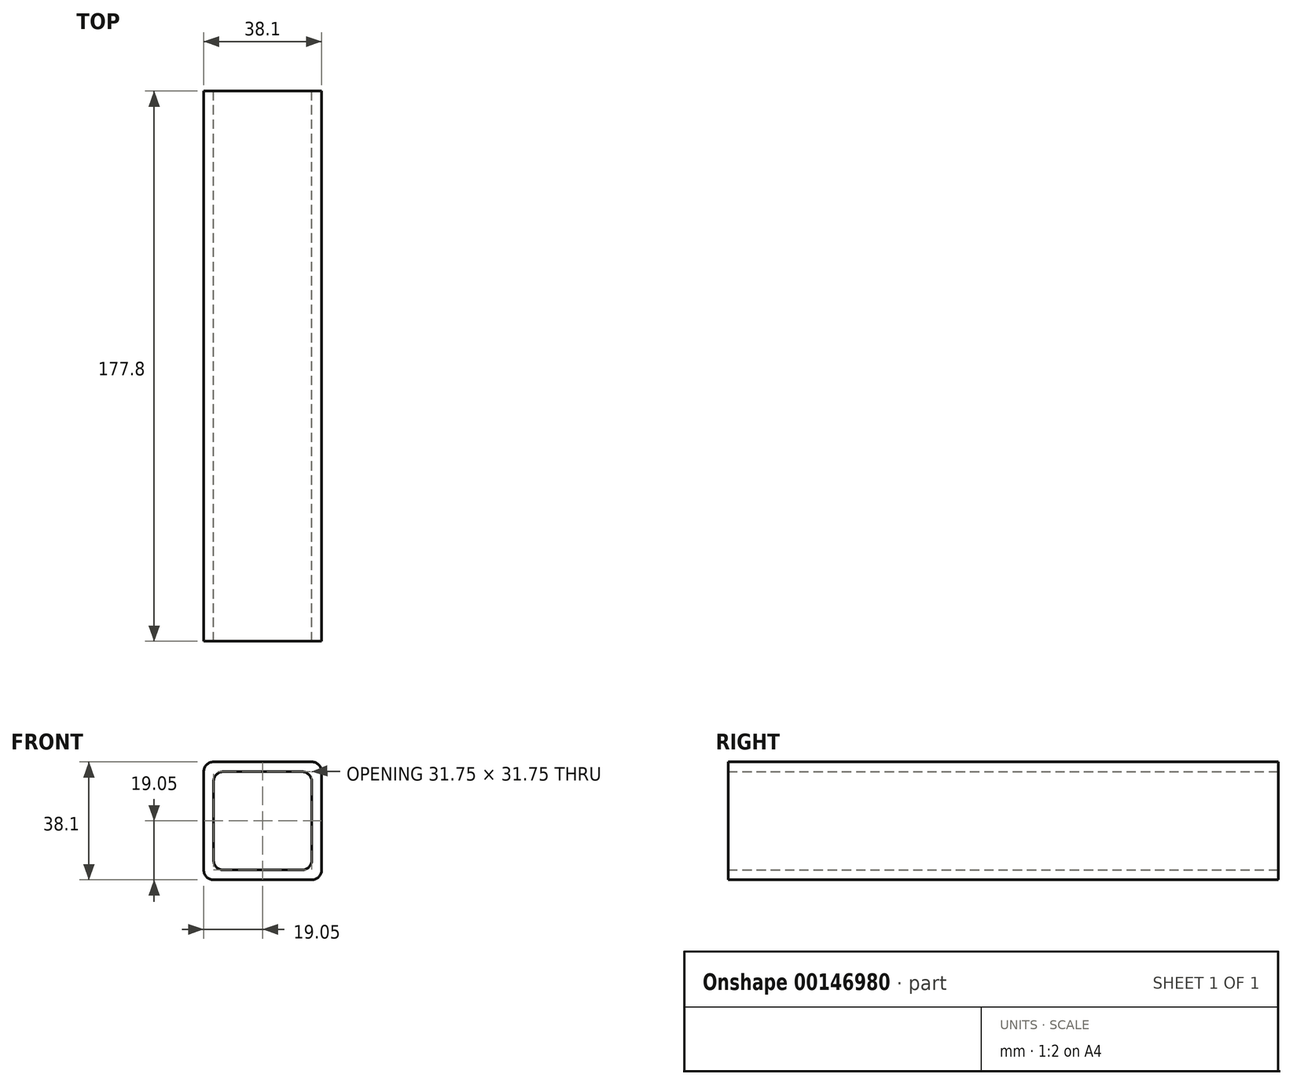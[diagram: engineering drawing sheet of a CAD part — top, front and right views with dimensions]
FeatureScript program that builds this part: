
annotation { "Feature Type Name" : "Feature", "Feature Type Description" : "" }
export const myFeature = defineFeature(function(context is Context, id is Id, definition is map)
    precondition{}
    {
        {
            var Q0;
            Q0=qCreatedBy(makeId("Front.planeOp"),FACE);
            var sketch = newSketch(context, id + "F0", { "sketchPlane" : qUnion([Q0])});
            skLineSegment(sketch, "E0.bottom", {"start": v(15.87, 19.05) * mm, "end": v(-15.87, 19.05) * mm});
            skLineSegment(sketch, "E0.top", {"start": v(15.87, -19.05) * mm, "end": v(-15.87, -19.05) * mm});
            skLineSegment(sketch, "E0.left", {"start": v(19.05, 15.87) * mm, "end": v(19.05, -15.87) * mm});
            skLineSegment(sketch, "E0.right", {"start": v(-19.05, 15.87) * mm, "end": v(-19.05, -15.87) * mm});
            skPoint(sketch, "E0.middle", {"position": v(0, 0) * mm});
            skPoint(sketch, "E1.visualSharp", {"position": v(-19.05, 19.05) * mm});
            skArc(sketch, "E1.filletArc", {"start": v(-15.87, 19.05) * mm, "mid": v(-18.12, 18.12) * mm, "end": v(-19.05, 15.87) * mm});
            skPoint(sketch, "E2.visualSharp", {"position": v(19.05, 19.05) * mm});
            skArc(sketch, "E2.filletArc", {"start": v(19.05, 15.87) * mm, "mid": v(18.12, 18.12) * mm, "end": v(15.87, 19.05) * mm});
            skPoint(sketch, "E3.visualSharp", {"position": v(-19.05, -19.05) * mm});
            skArc(sketch, "E3.filletArc", {"start": v(-19.05, -15.87) * mm, "mid": v(-18.12, -18.12) * mm, "end": v(-15.87, -19.05) * mm});
            skPoint(sketch, "E4.visualSharp", {"position": v(19.05, -19.05) * mm});
            skArc(sketch, "E4.filletArc", {"start": v(15.87, -19.05) * mm, "mid": v(18.12, -18.12) * mm, "end": v(19.05, -15.87) * mm});
            skLineSegment(sketch, "E5.bottom", {"start": v(12.7, 15.88) * mm, "end": v(-12.7, 15.88) * mm});
            skLineSegment(sketch, "E5.top", {"start": v(12.7, -15.88) * mm, "end": v(-12.7, -15.88) * mm});
            skLineSegment(sketch, "E5.left", {"start": v(15.88, 12.7) * mm, "end": v(15.88, -12.7) * mm});
            skLineSegment(sketch, "E5.right", {"start": v(-15.88, 12.7) * mm, "end": v(-15.88, -12.7) * mm});
            skPoint(sketch, "E6.visualSharp", {"position": v(-15.87, 15.88) * mm});
            skArc(sketch, "E6.filletArc", {"start": v(-12.7, 15.88) * mm, "mid": v(-14.95, 14.95) * mm, "end": v(-15.88, 12.7) * mm});
            skPoint(sketch, "E7.visualSharp", {"position": v(15.88, 15.88) * mm});
            skArc(sketch, "E7.filletArc", {"start": v(15.88, 12.7) * mm, "mid": v(14.95, 14.95) * mm, "end": v(12.7, 15.88) * mm});
            skPoint(sketch, "E8.visualSharp", {"position": v(-15.88, -15.88) * mm});
            skArc(sketch, "E8.filletArc", {"start": v(-15.88, -12.7) * mm, "mid": v(-14.95, -14.95) * mm, "end": v(-12.7, -15.88) * mm});
            skPoint(sketch, "E9.visualSharp", {"position": v(15.87, -15.88) * mm});
            skArc(sketch, "E9.filletArc", {"start": v(12.7, -15.88) * mm, "mid": v(14.95, -14.95) * mm, "end": v(15.88, -12.7) * mm});
            skSolve(sketch);
        }
        {
            var Q0;
            Q0 = qSketchRegion(id + "F0", true);
            extrude(context, id + "F1", {"entities" : qUnion([Q0]), "depth" : 177.8 * mm});
        }
    });
